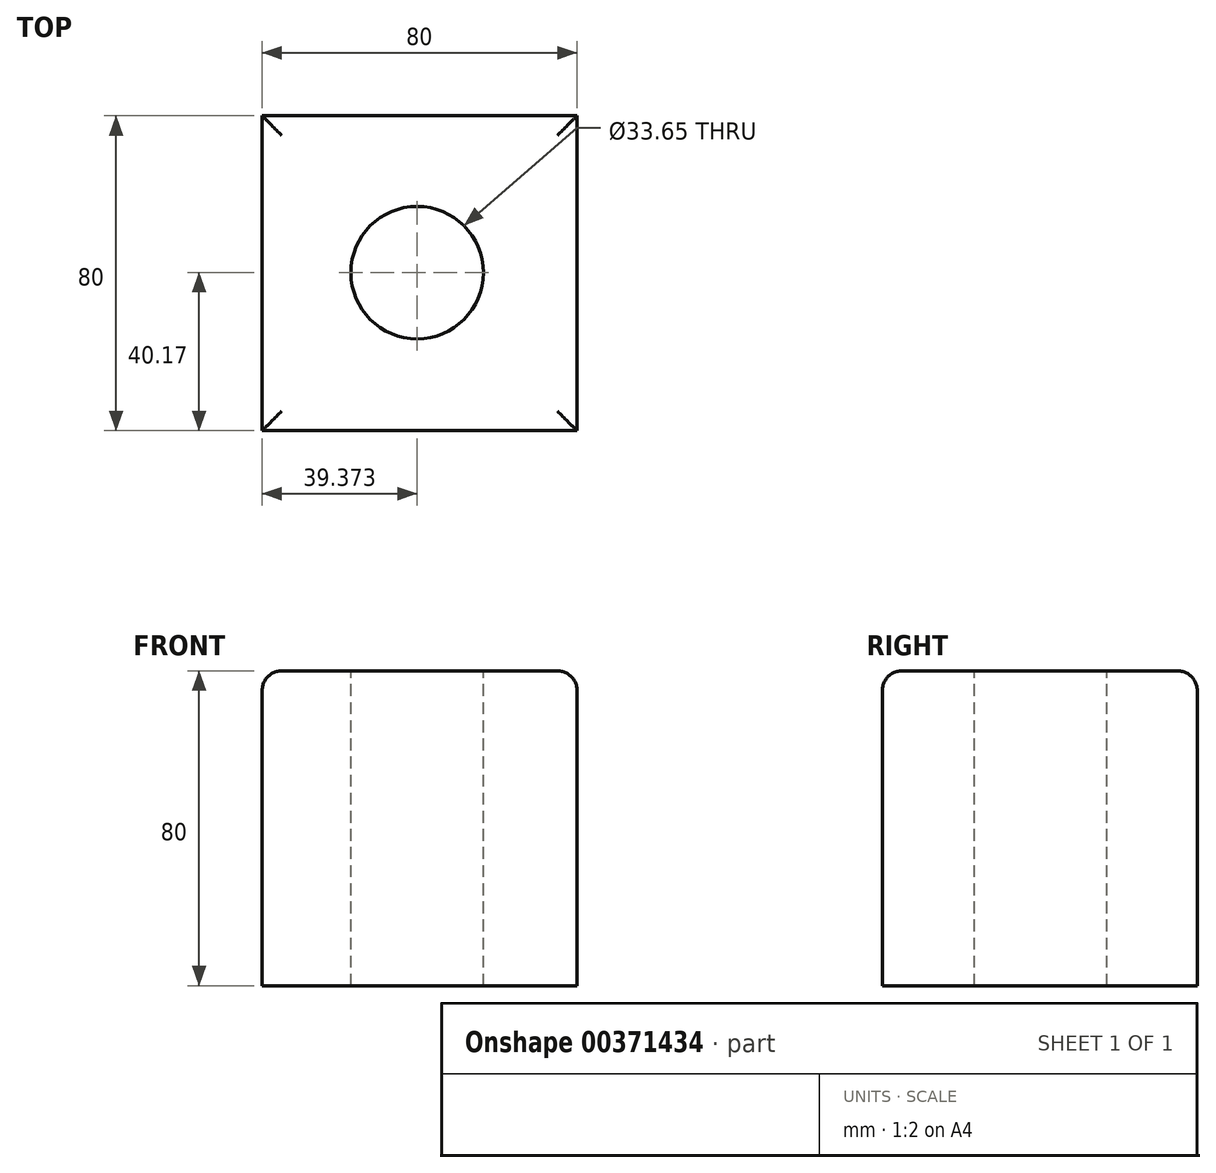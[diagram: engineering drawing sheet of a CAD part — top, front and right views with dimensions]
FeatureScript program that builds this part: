
annotation { "Feature Type Name" : "Feature", "Feature Type Description" : "" }
export const myFeature = defineFeature(function(context is Context, id is Id, definition is map)
    precondition{}
    {
        {
            var Q0;
            Q0=qCreatedBy(makeId("Top.planeOp"),FACE);
            var sketch = newSketch(context, id + "F0", { "sketchPlane" : qUnion([Q0])});
            skLineSegment(sketch, "E0.bottom", {"start": v(-94.95, 67.58) * mm, "end": v(-14.95, 67.58) * mm});
            skLineSegment(sketch, "E0.top", {"start": v(-94.95, -12.42) * mm, "end": v(-14.95, -12.42) * mm});
            skLineSegment(sketch, "E0.left", {"start": v(-94.95, 67.58) * mm, "end": v(-94.95, -12.42) * mm});
            skLineSegment(sketch, "E0.right", {"start": v(-14.95, 67.58) * mm, "end": v(-14.95, -12.42) * mm});
            skSolve(sketch);
        }
        {
            var Q0;
            Q0=makeQuery(id+"F0.imprint","IMPRINT",FACE,{"disambiguationData":[TD([[makeQuery(id+"F0.imprint","IMPRINT",EDGE,{"derivedFrom":sQuery(id+"F0.wireOp",EDGE,"E0.bottom")}),-1.0]])]});
            extrude(context, id + "F1", {"entities" : qUnion([Q0]), "depth" : 80 * mm});
        }
        {
            var Q0;
            Q0=makeQuery(id+"F1.opExtrude","CAP_FACE",FACE,{"disambiguationData":[OSD([sQuery(id+"F0.wireOp",EDGE,"E0.bottom"),sQuery(id+"F0.wireOp",EDGE,"E0.top"),sQuery(id+"F0.wireOp",EDGE,"E0.left"),sQuery(id+"F0.wireOp",EDGE,"E0.right")])],"isStart":false});
            var sketch = newSketch(context, id + "F2", { "sketchPlane" : qUnion([Q0])});
            skCircle(sketch, "E1", {"center": v(-55.58, 27.75) * mm, "radius": 16.82 * mm});
            skSolve(sketch);
        }
        {
            var Q0;
            Q0=makeQuery(id+"F2.imprint","IMPRINT",FACE,{"disambiguationData":[TD([[makeQuery(id+"F2.imprint","IMPRINT",EDGE,{"derivedFrom":sQuery(id+"F2.wireOp",EDGE,"E1")}),1.0]])]});
            extrude(context, id + "F3", {"entities" : qUnion([Q0]), "operationType" : NewBodyOperationType.REMOVE, "endBound" : BoundingType.THROUGH_ALL, "oppositeDirection" : true, "depth" : 25 * mm});
        }
        {
            var Q0;
            Q0=makeQuery(id+"F1.opExtrude","CAP_EDGE",EDGE,{"disambiguationData":[OSD([sQuery(id+"F0.wireOp",EDGE,"E0.bottom")])],"isStart":false});
            var Q1;
            Q1=makeQuery(id+"F1.opExtrude","CAP_EDGE",EDGE,{"disambiguationData":[OSD([sQuery(id+"F0.wireOp",EDGE,"E0.left")])],"isStart":false});
            var Q2;
            Q2=makeQuery(id+"F1.opExtrude","CAP_EDGE",EDGE,{"disambiguationData":[OSD([sQuery(id+"F0.wireOp",EDGE,"E0.top")])],"isStart":false});
            var Q3;
            Q3=makeQuery(id+"F1.opExtrude","CAP_EDGE",EDGE,{"disambiguationData":[OSD([sQuery(id+"F0.wireOp",EDGE,"E0.right")])],"isStart":false});
            fillet(context, id + "F4", {"entities" : qUnion([Q0, Q1, Q2, Q3]), "radius" : 5 * mm, "tangentPropagation" : true, "allowEdgeOverflow" : false});
        }
    });
